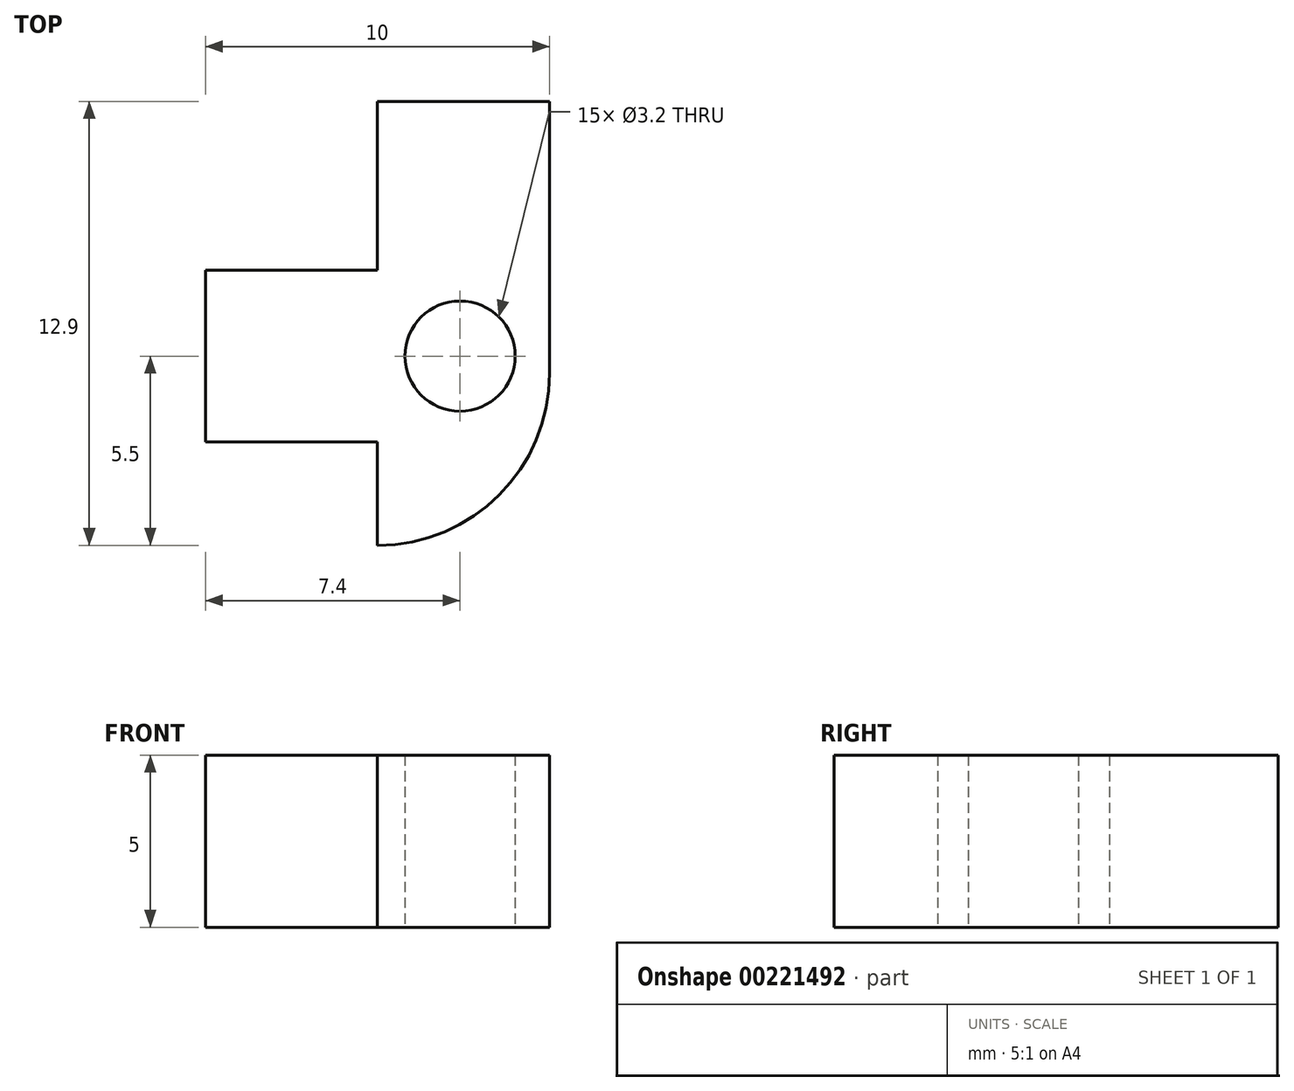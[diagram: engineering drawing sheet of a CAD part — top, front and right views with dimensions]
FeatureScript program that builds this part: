
annotation { "Feature Type Name" : "Feature", "Feature Type Description" : "" }
export const myFeature = defineFeature(function(context is Context, id is Id, definition is map)
    precondition{}
    {
        {
            var Q0;
            Q0=qCreatedBy(makeId("Top.planeOp"),FACE);
            var sketch = newSketch(context, id + "F0", { "sketchPlane" : qUnion([Q0])});
            skLineSegment(sketch, "E0.bottom", {"start": v(0, 0) * mm, "end": v(5, 0) * mm});
            skLineSegment(sketch, "E0.top", {"start": v(0, 5) * mm, "end": v(5, 5) * mm});
            skLineSegment(sketch, "E0.left", {"start": v(0, 0) * mm, "end": v(0, 5) * mm});
            skLineSegment(sketch, "E0.right", {"start": v(10, 2) * mm, "end": v(10, 9.9) * mm});
            skLineSegment(sketch, "E1", {"start": v(5, 5) * mm, "end": v(5, 0) * mm, "construction": true});
            skCircle(sketch, "E2", {"center": v(7.4, 2.5) * mm, "radius": 1.6 * mm});
            skPoint(sketch, "E2.centerSnap0", {"position": v(5, 2.5) * mm});
            skLineSegment(sketch, "E3", {"start": v(5, 5) * mm, "end": v(5, 9.9) * mm});
            skLineSegment(sketch, "E4", {"start": v(5, 9.9) * mm, "end": v(5, 9.9) * mm});
            skLineSegment(sketch, "E5", {"start": v(5, 0) * mm, "end": v(5, -3) * mm});
            skLineSegment(sketch, "E6", {"start": v(5, -3) * mm, "end": v(5, -3) * mm});
            skPoint(sketch, "E7.visualSharp", {"position": v(10, -3) * mm});
            skArc(sketch, "E7.filletArc", {"start": v(5, -3) * mm, "mid": v(8.54, -1.54) * mm, "end": v(10, 2) * mm});
            skLineSegment(sketch, "E8", {"start": v(5, 9.9) * mm, "end": v(10, 9.9) * mm});
            skSolve(sketch);
        }
        {
            var Q0;
            Q0=makeQuery(id+"F0.imprint","IMPRINT",FACE,{"disambiguationData":[TD([[makeQuery(id+"F0.imprint","IMPRINT",EDGE,{"derivedFrom":sQuery(id+"F0.wireOp",EDGE,"E0.bottom")}),1.0]])]});
            extrude(context, id + "F1", {"entities" : qUnion([Q0]), "depth" : 5 * mm});
        }
    });
